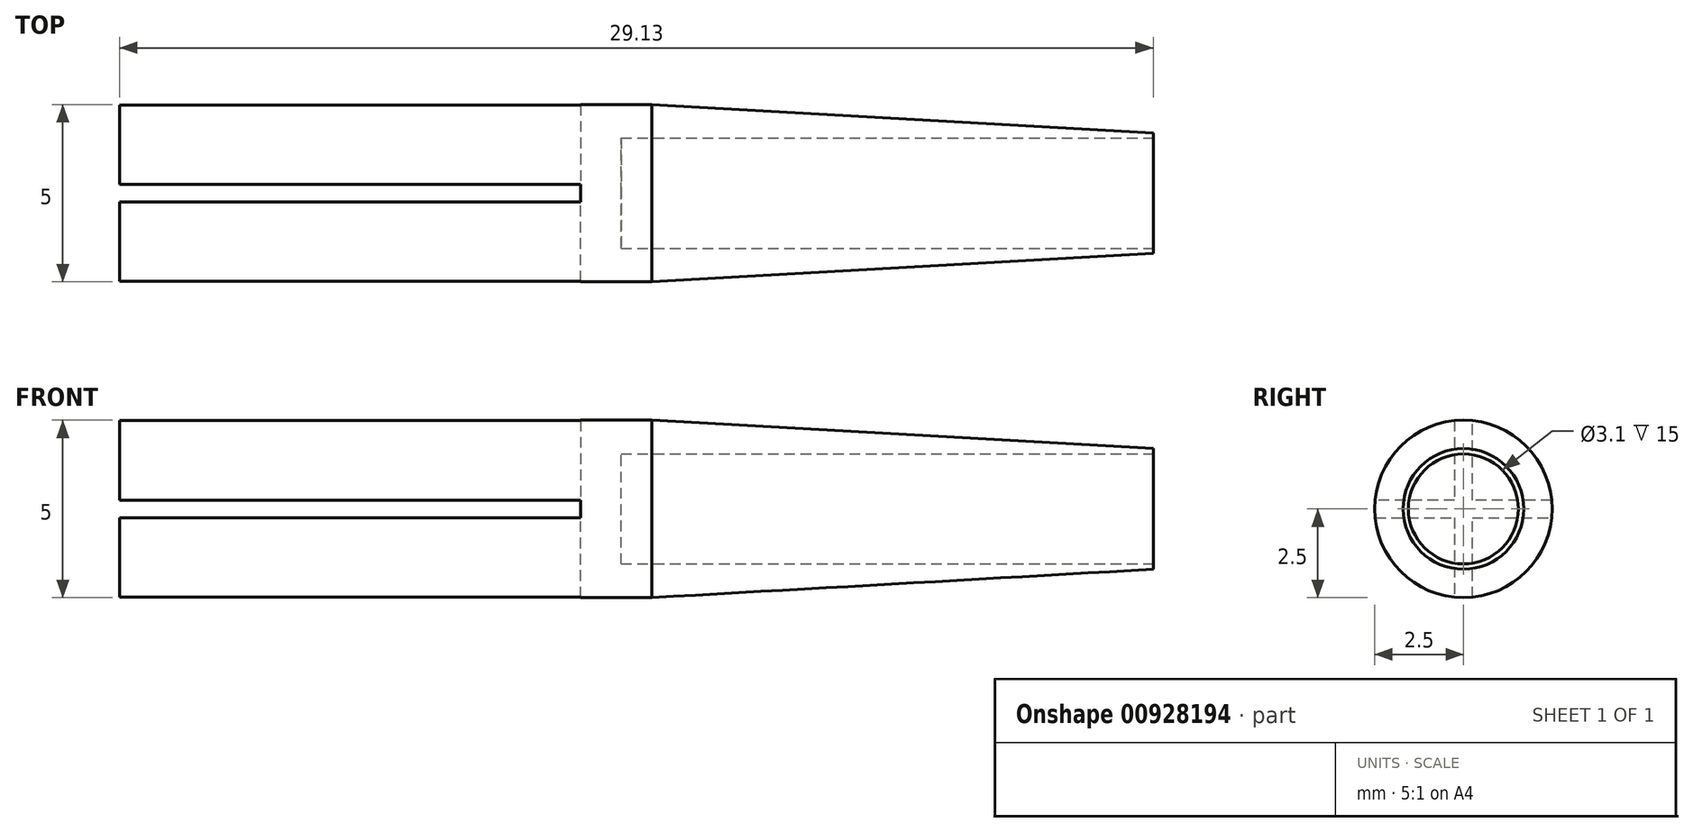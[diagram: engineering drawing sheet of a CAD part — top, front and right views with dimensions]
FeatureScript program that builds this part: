
annotation { "Feature Type Name" : "Feature", "Feature Type Description" : "" }
export const myFeature = defineFeature(function(context is Context, id is Id, definition is map)
    precondition{}
    {
        {
            var Q0;
            Q0=qCreatedBy(makeId("Front.planeOp"),FACE);
            var sketch = newSketch(context, id + "F0", { "sketchPlane" : qUnion([Q0])});
            skLineSegment(sketch, "E0", {"start": v(-29.13, 0) * mm, "end": v(-29.13, 2.5) * mm});
            skLineSegment(sketch, "E1", {"start": v(-29.13, 2.5) * mm, "end": v(-14.13, 2.5) * mm});
            skLineSegment(sketch, "E2", {"start": v(0, 0) * mm, "end": v(-29.13, 0) * mm});
            skLineSegment(sketch, "E3", {"start": v(0, 0) * mm, "end": v(0, 1.7) * mm});
            skLineSegment(sketch, "E4", {"start": v(0, 1.7) * mm, "end": v(-14.13, 2.5) * mm});
            skSolve(sketch);
        }
        {
            var Q0;
            Q0 = qSketchRegion(id + "F0", true);
            var Q1;
            Q1=sQuery(id+"F0.wireOp",EDGE,"E2");
            revolve(context, id + "F1", {"surfaceOperationType" : NewSurfaceOperationType.NEW, "entities" : qUnion([Q0]), "axis" : qUnion([Q1]), "revolveType" : RevolveType.FULL});
        }
        {
            var Q0;
            Q0=qCreatedBy(makeId("Right.planeOp"),FACE);
            var sketch = newSketch(context, id + "F2", { "sketchPlane" : qUnion([Q0])});
            skCircle(sketch, "E5", {"center": v(0, 0) * mm, "radius": 1.55 * mm});
            skSolve(sketch);
        }
        {
            var Q0;
            Q0 = qSketchRegion(id + "F2", true);
            extrude(context, id + "F3", {"entities" : qUnion([Q0]), "operationType" : NewBodyOperationType.REMOVE, "oppositeDirection" : true, "depth" : 15 * mm, "offsetDistance" : 25 * mm});
        }
        {
            var Q0;
            Q0=makeQuery(id+"F1.opRevolve","SWEPT_FACE",FACE,{"disambiguationData":[OSD([sQuery(id+"F0.wireOp",EDGE,"E0")])]});
            var sketch = newSketch(context, id + "F4", { "sketchPlane" : qUnion([Q0])});
            skLineSegment(sketch, "E6", {"start": v(-2.93, 0) * mm, "end": v(-2.93, 0.25) * mm});
            skLineSegment(sketch, "E7", {"start": v(-2.93, 0.25) * mm, "end": v(-0.25, 0.25) * mm});
            skLineSegment(sketch, "E8", {"start": v(3.68, 0.25) * mm, "end": v(3.68, -0.25) * mm});
            skLineSegment(sketch, "E9", {"start": v(3.68, -0.25) * mm, "end": v(0.25, -0.25) * mm});
            skLineSegment(sketch, "E10", {"start": v(-2.93, -0.25) * mm, "end": v(-2.93, 0) * mm});
            skLineSegment(sketch, "E11", {"start": v(0.25, 2.97) * mm, "end": v(0.25, 0.25) * mm});
            skLineSegment(sketch, "E12", {"start": v(0.25, -2.63) * mm, "end": v(-0.25, -2.63) * mm});
            skLineSegment(sketch, "E13", {"start": v(-0.25, -2.63) * mm, "end": v(-0.25, -0.25) * mm});
            skPoint(sketch, "E14.start.orphan", {"position": v(0, 2.97) * mm});
            skLineSegment(sketch, "E15", {"start": v(0.25, 2.97) * mm, "end": v(-0.25, 2.97) * mm});
            skLineSegment(sketch, "E16.trimOffspring", {"start": v(0.25, -0.25) * mm, "end": v(0.25, -2.63) * mm});
            skLineSegment(sketch, "E17.trimOffspring", {"start": v(-0.25, 0.25) * mm, "end": v(-0.25, 2.97) * mm});
            skLineSegment(sketch, "E18.trimOffspring", {"start": v(0.25, 0.25) * mm, "end": v(3.68, 0.25) * mm});
            skLineSegment(sketch, "E19.trimOffspring", {"start": v(-0.25, -0.25) * mm, "end": v(-2.93, -0.25) * mm});
            skSolve(sketch);
        }
        {
            var Q0;
            Q0 = qSketchRegion(id + "F4", true);
            extrude(context, id + "F5", {"entities" : qUnion([Q0]), "operationType" : NewBodyOperationType.REMOVE, "oppositeDirection" : true, "depth" : 13 * mm, "offsetDistance" : 25 * mm});
        }
    });
